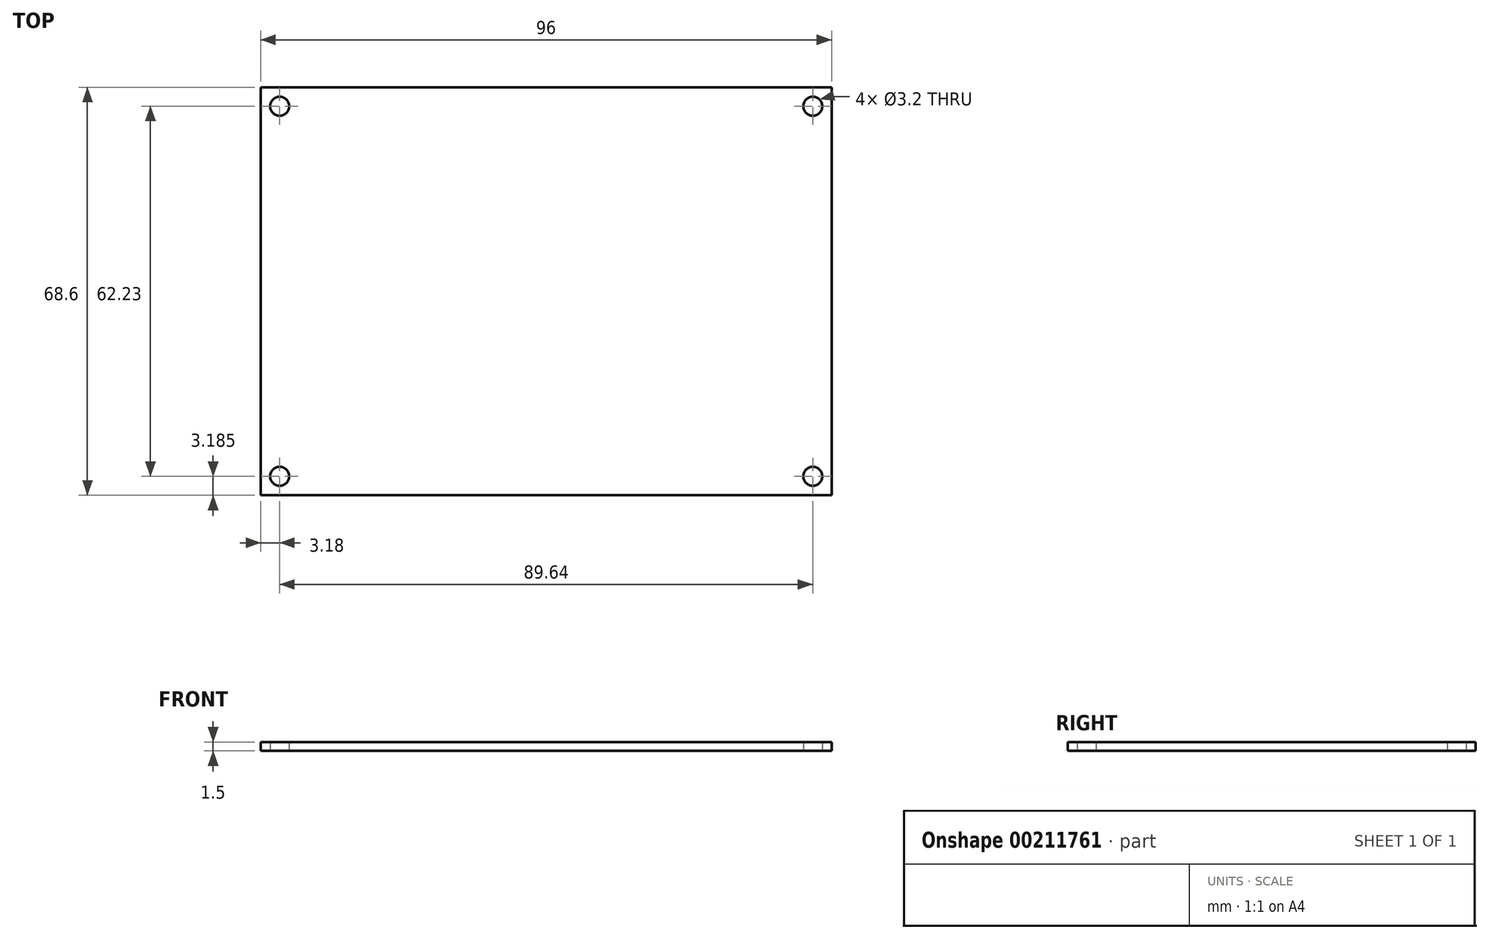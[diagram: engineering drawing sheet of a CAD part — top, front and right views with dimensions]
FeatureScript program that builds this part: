
annotation { "Feature Type Name" : "Feature", "Feature Type Description" : "" }
export const myFeature = defineFeature(function(context is Context, id is Id, definition is map)
    precondition{}
    {
        {
            var Q0;
            Q0=qCreatedBy(makeId("Top.planeOp"),FACE);
            var sketch = newSketch(context, id + "F0", { "sketchPlane" : qUnion([Q0])});
            skLineSegment(sketch, "E0.bottom", {"start": v(48, -34.3) * mm, "end": v(-48, -34.3) * mm});
            skLineSegment(sketch, "E0.top", {"start": v(48, 34.3) * mm, "end": v(-48, 34.3) * mm});
            skLineSegment(sketch, "E0.left", {"start": v(48, -34.3) * mm, "end": v(48, 34.3) * mm});
            skLineSegment(sketch, "E0.right", {"start": v(-48, -34.3) * mm, "end": v(-48, 34.3) * mm});
            skPoint(sketch, "E0.middle", {"position": v(0, 0) * mm});
            skCircle(sketch, "E1", {"center": v(-44.82, -31.12) * mm, "radius": 1.6 * mm});
            skLineSegment(sketch, "E2", {"start": v(0, 34.3) * mm, "end": v(0, -34.3) * mm, "construction": true});
            skLineSegment(sketch, "E3", {"start": v(-48, 0) * mm, "end": v(48, 0) * mm, "construction": true});
            skCircle(sketch, "E4.MirrorC", {"center": v(44.82, -31.12) * mm, "radius": 1.6 * mm});
            skCircle(sketch, "E5.MirrorC", {"center": v(-44.82, 31.11) * mm, "radius": 1.6 * mm});
            skCircle(sketch, "E6.MirrorC", {"center": v(44.82, 31.12) * mm, "radius": 1.6 * mm});
            skSolve(sketch);
        }
        {
            var Q0;
            Q0=makeQuery(id+"F0.imprint","IMPRINT",FACE,{"disambiguationData":[TD([[makeQuery(id+"F0.imprint","IMPRINT",EDGE,{"derivedFrom":sQuery(id+"F0.wireOp",EDGE,"E0.bottom")}),-1.0]])]});
            extrude(context, id + "F1", {"entities" : qUnion([Q0]), "depth" : 1.5 * mm});
        }
    });
